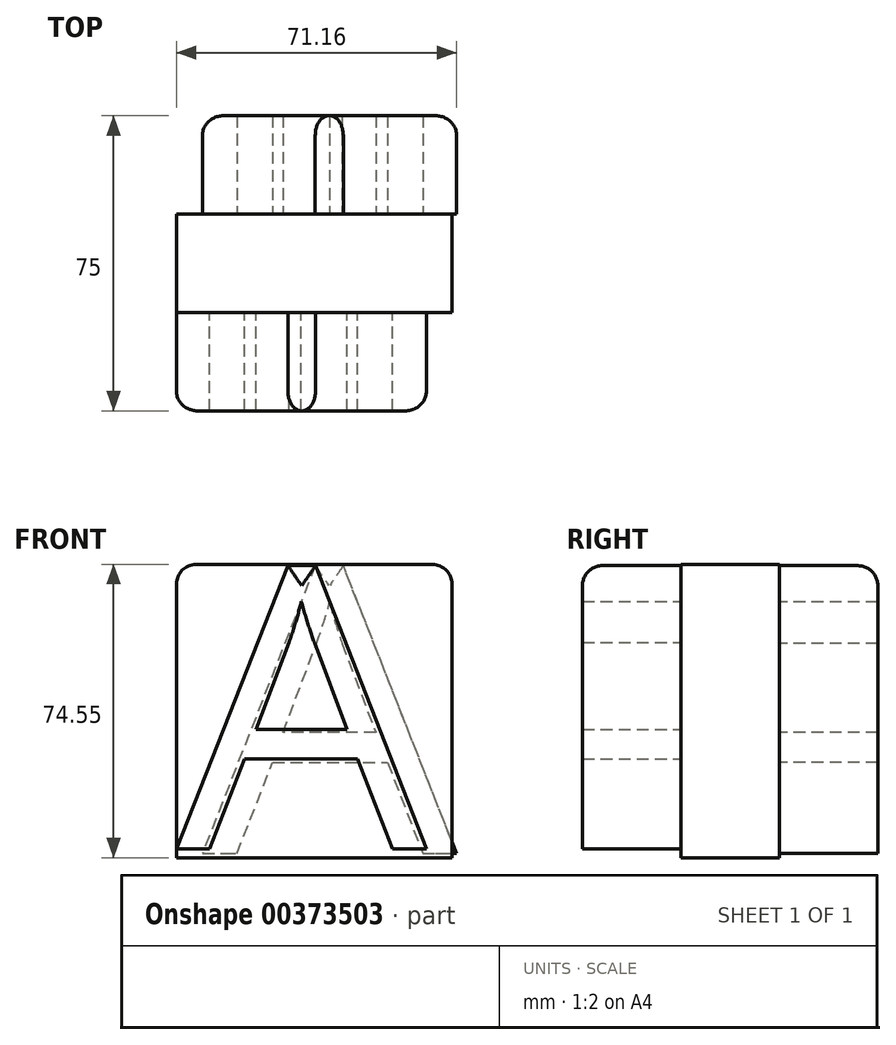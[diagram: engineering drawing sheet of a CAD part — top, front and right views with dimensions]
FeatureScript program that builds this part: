
annotation { "Feature Type Name" : "Feature", "Feature Type Description" : "" }
export const myFeature = defineFeature(function(context is Context, id is Id, definition is map)
    precondition{}
    {
        {
            var Q0;
            Q0=qCreatedBy(makeId("Front.planeOp"),FACE);
            var sketch = newSketch(context, id + "F0", { "sketchPlane" : qUnion([Q0])});
            skText(sketch, "E0", { "text": "A\n", "fontName": "OpenSans-Regular.ttf"});
            const initialGuessF0  = {"E0": [-0.07, -0.07224, 1, 0, 0.07224]};
            skSetInitialGuess(sketch, initialGuessF0);
            skSolve(sketch);
        }
        {
            var Q0;
            Q0 = qSketchRegion(id + "F0", true);
            extrude(context, id + "F1", {"entities" : qUnion([Q0]), "depth" : 25 * mm});
        }
        {
            var Q0;
            Q0=qCreatedBy(makeId("Front.planeOp"),FACE);
            var sketch = newSketch(context, id + "F2", { "sketchPlane" : qUnion([Q0])});
            skLineSegment(sketch, "E1.bottom", {"start": v(0, 0) * mm, "end": v(-70, 0) * mm});
            skLineSegment(sketch, "E1.top", {"start": v(0, -74.55) * mm, "end": v(-70, -74.55) * mm});
            skLineSegment(sketch, "E1.left", {"start": v(0, 0) * mm, "end": v(0, -74.55) * mm});
            skLineSegment(sketch, "E1.right", {"start": v(-70, 0) * mm, "end": v(-70, -74.55) * mm});
            skSolve(sketch);
        }
        {
            var Q0;
            Q0=makeQuery(id+"F2.imprint","IMPRINT",FACE,{"disambiguationData":[TD([[makeQuery(id+"F2.imprint","IMPRINT",EDGE,{"derivedFrom":sQuery(id+"F2.wireOp",EDGE,"E1.bottom")}),1.0]])]});
            var Q1;
            Q1=makeQuery(id+"F1.opExtrude","CAP_FACE",FACE,{"disambiguationData":[OSD([sQuery(id+"F0.wireOp",EDGE,"E0.sketch_text.stroke-0"),sQuery(id+"F0.wireOp",EDGE,"E0.sketch_text.stroke-1"),sQuery(id+"F0.wireOp",EDGE,"E0.sketch_text.stroke-2"),sQuery(id+"F0.wireOp",EDGE,"E0.sketch_text.stroke-3"),sQuery(id+"F0.wireOp",EDGE,"E0.sketch_text.stroke-4"),sQuery(id+"F0.wireOp",EDGE,"E0.sketch_text.stroke-5"),sQuery(id+"F0.wireOp",EDGE,"E0.sketch_text.stroke-6"),sQuery(id+"F0.wireOp",EDGE,"E0.sketch_text.stroke-7"),sQuery(id+"F0.wireOp",EDGE,"E0.sketch_text.stroke-8"),sQuery(id+"F0.wireOp",EDGE,"E0.sketch_text.stroke-9"),sQuery(id+"F0.wireOp",EDGE,"E0.sketch_text.stroke-10"),sQuery(id+"F0.wireOp",EDGE,"E0.sketch_text.stroke-11"),sQuery(id+"F0.wireOp",EDGE,"E0.sketch_text.stroke-12")])],"isStart":false});
            extrude(context, id + "F3", {"entities" : qUnion([Q0, Q1]), "operationType" : NewBodyOperationType.ADD, "depth" : 25 * mm});
        }
        {
            var Q0;
            Q0=qCreatedBy(makeId("Right.planeOp"),FACE);
            var sketch = newSketch(context, id + "F4", { "sketchPlane" : qUnion([Q0])});
            skLineSegment(sketch, "E2.0.0", {"start": v(0, -74.55) * mm, "end": v(0, 0) * mm});
            skLineSegment(sketch, "E2.0.1", {"start": v(0, 0) * mm, "end": v(-25, 0) * mm});
            skLineSegment(sketch, "E2.0.2", {"start": v(-25, 0) * mm, "end": v(-25, -74.55) * mm});
            skLineSegment(sketch, "E2.0.3", {"start": v(-25, -74.55) * mm, "end": v(0, -74.55) * mm});
            skSolve(sketch);
        }
        {
            var Q0;
            Q0=makeQuery(id+"F3.boolean.opBoolean","MERGE",FACE,{"derivedFrom":[makeQuery(id+"F1.opExtrude","CAP_FACE",FACE,{"disambiguationData":[OSD([sQuery(id+"F0.wireOp",EDGE,"E0.sketch_text.stroke-0"),sQuery(id+"F0.wireOp",EDGE,"E0.sketch_text.stroke-1"),sQuery(id+"F0.wireOp",EDGE,"E0.sketch_text.stroke-2"),sQuery(id+"F0.wireOp",EDGE,"E0.sketch_text.stroke-3"),sQuery(id+"F0.wireOp",EDGE,"E0.sketch_text.stroke-4"),sQuery(id+"F0.wireOp",EDGE,"E0.sketch_text.stroke-5"),sQuery(id+"F0.wireOp",EDGE,"E0.sketch_text.stroke-6"),sQuery(id+"F0.wireOp",EDGE,"E0.sketch_text.stroke-7"),sQuery(id+"F0.wireOp",EDGE,"E0.sketch_text.stroke-8"),sQuery(id+"F0.wireOp",EDGE,"E0.sketch_text.stroke-9"),sQuery(id+"F0.wireOp",EDGE,"E0.sketch_text.stroke-10"),sQuery(id+"F0.wireOp",EDGE,"E0.sketch_text.stroke-11"),sQuery(id+"F0.wireOp",EDGE,"E0.sketch_text.stroke-12")])],"isStart":true}),makeQuery(id+"F3.opExtrude","CAP_FACE",FACE,{"disambiguationData":[OSD([sQuery(id+"F2.wireOp",EDGE,"E1.bottom"),sQuery(id+"F2.wireOp",EDGE,"E1.top"),sQuery(id+"F2.wireOp",EDGE,"E1.left"),sQuery(id+"F2.wireOp",EDGE,"E1.right")])],"isStart":true})]});
            var sketch = newSketch(context, id + "F5", { "sketchPlane" : qUnion([Q0])});
            skText(sketch, "E3", { "text": "A", "fontName": "OpenSans-Regular.ttf"});
            const initialGuessF5  = {"E3": [-0.00116, -0.07344, 1, 0, 0.07344]};
            skSetInitialGuess(sketch, initialGuessF5);
            skSolve(sketch);
        }
        {
            var Q0;
            Q0 = qSketchRegion(id + "F5", true);
            extrude(context, id + "F6", {"entities" : qUnion([Q0]), "operationType" : NewBodyOperationType.ADD, "depth" : 25 * mm});
        }
        {
            var Q0;
            Q0=makeQuery(id+"F3.opExtrude","SWEPT_EDGE",EDGE,{"disambiguationData":[OSD([sQuery(id+"F2.wireOp",EDGE,"E1.bottom"),sQuery(id+"F2.wireOp",EDGE,"E1.right")])]});
            var Q1;
            Q1=makeQuery(id+"F3.opExtrude","SWEPT_EDGE",EDGE,{"disambiguationData":[OSD([sQuery(id+"F2.wireOp",EDGE,"E1.bottom"),sQuery(id+"F2.wireOp",EDGE,"E1.left")])]});
            fillet(context, id + "F7", {"entities" : qUnion([Q0, Q1]), "radius" : 5 * mm, "tangentPropagation" : true, "allowEdgeOverflow" : false});
        }
        {
            var Q0;
            Q0=makeQuery(id+"F3.opExtrude","CAP_EDGE",EDGE,{"disambiguationData":[OSD([sQuery(id+"F0.wireOp",EDGE,"E0.sketch_text.stroke-5")])],"isStart":false});
            var Q1;
            Q1=makeQuery(id+"F6.opExtrude","CAP_EDGE",EDGE,{"disambiguationData":[OSD([sQuery(id+"F5.wireOp",EDGE,"E3.sketch_text.stroke-5")])],"isStart":false});
            var Q2;
            Q2=makeQuery(id+"F6.opExtrude","CAP_EDGE",EDGE,{"disambiguationData":[OSD([sQuery(id+"F5.wireOp",EDGE,"E3.sketch_text.stroke-6")])],"isStart":false});
            var Q3;
            Q3=makeQuery(id+"F6.opExtrude","CAP_EDGE",EDGE,{"disambiguationData":[OSD([sQuery(id+"F5.wireOp",EDGE,"E3.sketch_text.stroke-4")])],"isStart":false});
            var Q4;
            Q4=makeQuery(id+"F3.opExtrude","CAP_EDGE",EDGE,{"disambiguationData":[OSD([sQuery(id+"F0.wireOp",EDGE,"E0.sketch_text.stroke-4")])],"isStart":false});
            var Q5;
            Q5=makeQuery(id+"F3.opExtrude","CAP_EDGE",EDGE,{"disambiguationData":[OSD([sQuery(id+"F0.wireOp",EDGE,"E0.sketch_text.stroke-6")])],"isStart":false});
            fillet(context, id + "F8", {"entities" : qUnion([Q0, Q1, Q2, Q3, Q4, Q5]), "radius" : 5 * mm, "tangentPropagation" : true, "allowEdgeOverflow" : false});
        }
    });
